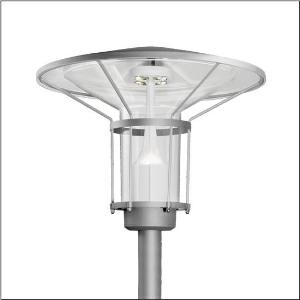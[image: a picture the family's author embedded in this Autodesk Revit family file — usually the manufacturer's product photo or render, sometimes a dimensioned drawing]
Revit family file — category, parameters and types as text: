
# Revit family: laterne_classic_iq___st1_2a_5xa5245mf14h_178e
name_source: partatom
category: Lighting Fixtures
units: mm (PartAtom-declared; Revit-internal decimal feet)

## family parameters
Cut with Voids When Loaded = No
Host = Face
Light Source = No
Part Type = Normal
Room Calculation Point = No
Round Connector Dimension = Use Diameter
Shared = No

## types (1)
- --- (1 x LED, 1380 lm, 11.8 W, 2700K)
    Apparent Load = 12 VA
    CIE Flux Codes = 21 60 93 97 100
    Color Rendering = 70
    Color Temperature = 2700K
    Default Elevation = 1800 mm
    Description = Lantern Classic iQ, mast luminaire, Module 540 iQ-SR, primary light control with 3 zone facetted reflector, of plastic, silver coated, highly specular, structured, primary optical cover: cover, of PMMA, transparent, light distribution: ST1.2a, light emission: direct distribution, primary light characteristic: asymmetric, installation type: post-top, LED, High Power LED, rated luminous flux: 1.380lm, luminous efficacy: 117lm/W, light colour: 727, colour temperature: 2700K, control gear: ECG iQ, control: presetting dimming logarithmic, Street-Remote, Auto-Match, Temp-Guard, Lumen-Switch, Night-Set, Smart-Wire, Light-Fading, Desk-Remote (wireless, voltage-free reading and setting of iQ features in the workshop via application-optimized NFC function/RFID function), optimised constant luminous flux control (CLO 2.0), with terminal, 6-pole, max. 2.5mm², mains connection: 230..240V, AC, 50/60Hz, start of lifetime: 12W, end of service life: 12W, reduction: 6W, luminaire housing, upper part, of glass-fibre reinforced polyester, coated, Siteco® metallic grey (DB 702S), diameter: 750mm, height: 596mm, spigot size: d x l = 76 x 70mm (post-top) | with reducer (optional accessory) 60 x 70mm, post-top mast mounting element, of diecast aluminium, coated, Siteco® metallic grey (DB 702S), Module 540 iQ-SR, traffic white (RAL 9016), equipment: standard, protection rating (complete): IP65, insulation class (complete): insulation class II (safety insulation), certification: CE, ENEC, VDE, packaging unit: 1 piece

Light Distribution: ST1.2a
    Height = 596 mm
    Lamp = 1 x LED
    Lamp Light Flux = 1380 lm
    Lamp Power = 11.8 W
    Lamp count = 1
    Length = 750 mm
    Luminous efficacy = 117 lm/W
    Manufacturer = Siteco
    ModVariant = No
    Model = 5XA5245MF14H
    Number of Poles = 1
    OnlyDefault = Yes
    Power Factor = 1
    Product Name = Laterne Classic iQ | ST1.2a
    Product group = mast luminaire | pylon top
    ProductGroupID = 6100
    Protection Class = Protection class II
    Protection Degree = IP 65
    RLX_Detail_Level = 1
    RLX_Emergency_Light_Flux = 0 lm
    RLX_Emergency_Type = 0
    RLX_Emergency_Type_DB = No
    RlxData = <blob elided: 91341 chars, md5=695da8b2>
    Socket = socket
    Standby Power = 0 W
    System Light Flux = 1380 lm
    System Power = 12 W
    Type Comments = factory setting: luminous flux: 100 % | dim-lin: 254 | 472 mA
    Type Image = l_1006052.jpg
    URL = http://relux.com
    VarID = @adj_085647
    Voltage = 0 V
    Weight = 0.00 kg
    Width = 0 mm  [stored 0 ft]

note: [stored X ft] marks values corroborated as IEEE doubles in the binary element streams (Revit-internal decimal feet)

## geometry (parser evidence)
native form markers: Blend x4, Sweep x11
no freeform markers — native parametric forms only
